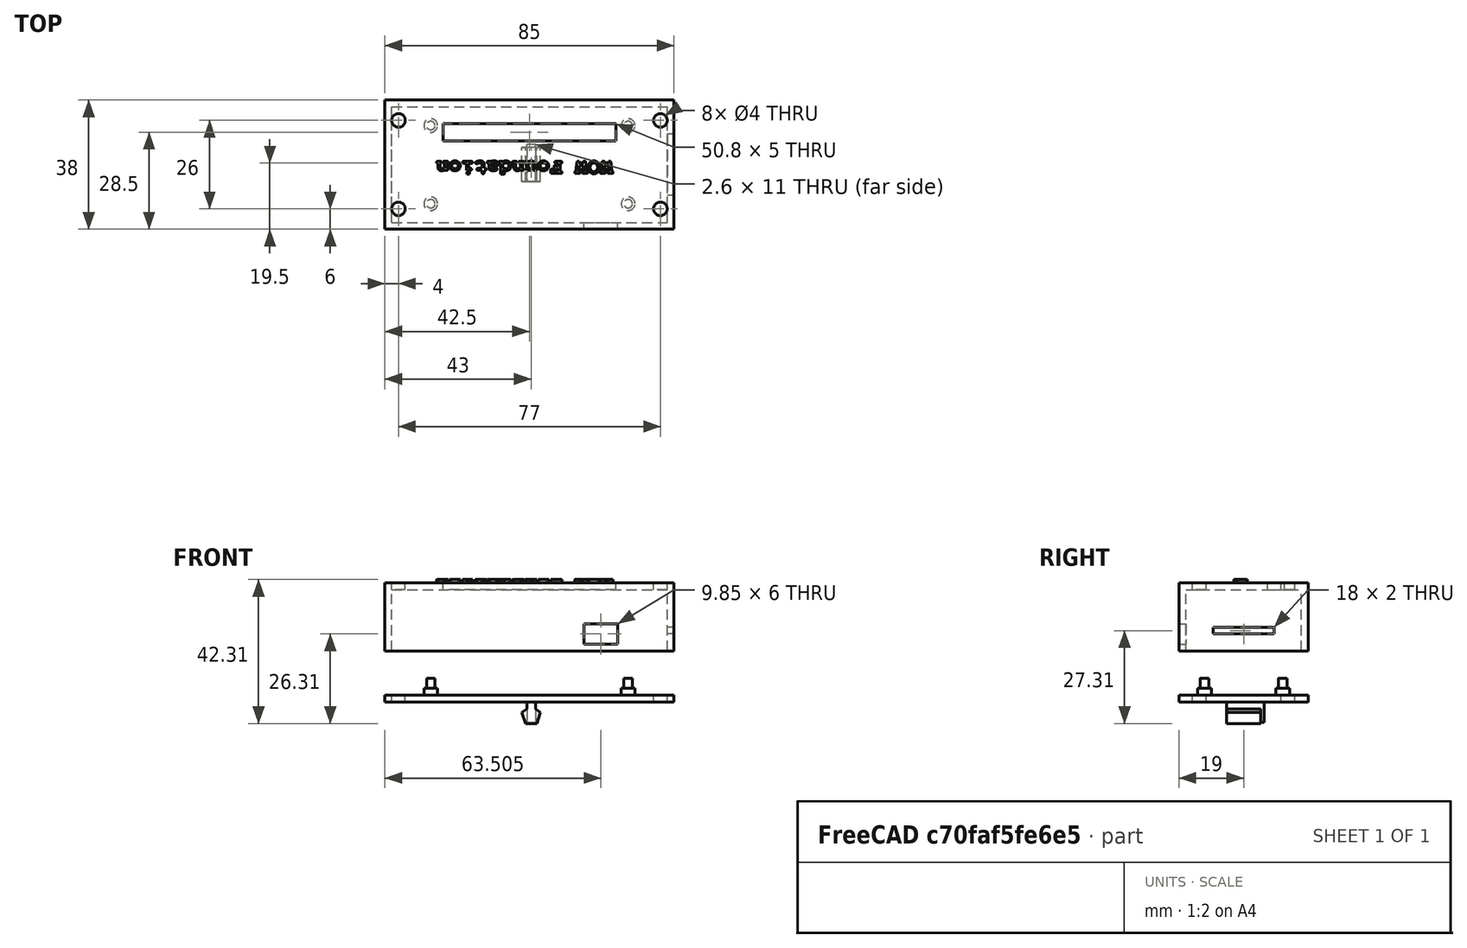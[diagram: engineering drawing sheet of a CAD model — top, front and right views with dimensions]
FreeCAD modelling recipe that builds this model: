
FCSTD DOCUMENT  (FreeCAD 0.18.1R)
Label: picase
License: All rights reserved
LicenseURL: http://en.wikipedia.org/wiki/All_rights_reserved
objects: Part::Cylinder×16, Part::Box×9, Part::MultiFuse×6, Part::Cut×6, Part::Extrusion×2, Part::Part2DObjectPython×1, Part::RegularPolygon×1
note: 41 computed .brp shape members not serialized (recipe doc carries the construction recipe); baked Part::Feature solids carry a one-line shape summary decoded from their .brp

FEATURE [Part::Box] Box  label="Cube"
  AttacherType = Attacher::AttachEngine3D
  Height = 2
  Length = 65
  Placement = pos=(0,-4,0) rot=(0,0,1;0rad)
  Width = 38
FEATURE [Part::Cylinder] Cylinder
  Angle = 360
  AttacherType = Attacher::AttachEngine3D
  Height = 5
  Placement = pos=(3.5,3.5,2) rot=(0,0,1;0rad)
  Radius = 1.25
FEATURE [Part::Cylinder] Cylinder001
  Angle = 360
  AttacherType = Attacher::AttachEngine3D
  Height = 5
  Placement = pos=(3.5,26.5,2) rot=(0,0,1;0rad)
  Radius = 1.25
FEATURE [Part::Cylinder] Cylinder002
  Angle = 360
  AttacherType = Attacher::AttachEngine3D
  Height = 5
  Placement = pos=(61.5,26.5,2) rot=(0,0,1;0rad)
  Radius = 1.25
FEATURE [Part::Cylinder] Cylinder003
  Angle = 360
  AttacherType = Attacher::AttachEngine3D
  Height = 5
  Placement = pos=(61.5,3.5,2) rot=(0,0,1;0rad)
  Radius = 1.25
FEATURE [Part::Box] Box001  label="Cube001"
  AttacherType = Attacher::AttachEngine3D
  Height = 2
  Length = 10
  Placement = pos=(-10,-4,0) rot=(0,0,1;0rad)
  Width = 38
FEATURE [Part::Box] Box002  label="Cube002"
  AttacherType = Attacher::AttachEngine3D
  Height = 2
  Length = 10
  Placement = pos=(65,-4,0) rot=(0,0,1;0rad)
  Width = 38
FEATURE [Part::Cylinder] Cylinder004
  Angle = 360
  AttacherType = Attacher::AttachEngine3D
  Height = 2
  Placement = pos=(3.5,3.5,2) rot=(0,0,1;0rad)
  Radius = 2
FEATURE [Part::Cylinder] Cylinder005
  Angle = 360
  AttacherType = Attacher::AttachEngine3D
  Height = 2
  Placement = pos=(3.5,26.5,2) rot=(0,0,1;0rad)
  Radius = 2
FEATURE [Part::Cylinder] Cylinder006
  Angle = 360
  AttacherType = Attacher::AttachEngine3D
  Height = 2
  Placement = pos=(61.5,26.5,2) rot=(0,0,1;0rad)
  Radius = 2
FEATURE [Part::Cylinder] Cylinder007
  Angle = 360
  AttacherType = Attacher::AttachEngine3D
  Height = 2
  Placement = pos=(61.5,3.5,2) rot=(0,0,1;0rad)
  Radius = 2
FEATURE [Part::MultiFuse] Fusion  label="Fusion - PI0W Base"
  Shapes = -> [Box,Cylinder003,Cylinder001,Box002,Cylinder002,Box001,Cylinder,Cylinder004,Cylinder005,Cylinder007,Cylinder006]
FEATURE [Part::Box] Box003  label="Micro-B USB"
  AttacherType = Attacher::AttachEngine3D
  Height = 6
  Length = 9.85
  Placement = pos=(48.58,-41,2) rot=(0,0,1;0rad)
  Width = 7
FEATURE [Part::Box] Box004  label="GPIOHeader"
  AttacherType = Attacher::AttachEngine3D
  Height = 10
  Length = 50.8
  Placement = pos=(7.1,-15,16) rot=(0,0,1;0rad)
  Width = 5
FEATURE [Part::Box] Box005  label="camera-cable-slot"
  AttacherType = Attacher::AttachEngine3D
  Height = 2
  Length = 18
  Placement = pos=(76,-31,5) rot=(0,0,1;1.5708rad)
  Width = 4
FEATURE [Part::Box] Box006  label="Pitop"
  AttacherType = Attacher::AttachEngine3D
  Height = 20
  Length = 85
  Placement = pos=(-10,-41,0) rot=(0,0,1;0rad)
  Width = 38
FEATURE [Part::Box] Box007  label="pihollow"
  AttacherType = Attacher::AttachEngine3D
  Height = 18
  Length = 81
  Placement = pos=(-8,-39,0) rot=(0,0,1;0rad)
  Width = 34
FEATURE [Part::Part2DObjectPython] ShapeString002  # Draft 2D object (typed FeaturePython)
  FontFile = <path>
  Placement = pos=(5,-40,11) rot=(0,0,1;0rad)
  Size = 2
  String = WOW Foundation
  Tracking = 0
FEATURE [Part::Extrusion] Extrude
  Base = -> ShapeString002
  Dir = (0,0,1)
  DirMode = 2
  FaceMakerClass = Part::FaceMakerBullseye
  LengthFwd = 2
  LengthRev = 0
  Placement = pos=(62,-61,8) rot=(0,0,1;3.14159rad)
  Solid = false
  Symmetric = false
FEATURE [Part::Box] Box008  label="Cube003"
  AttacherType = Attacher::AttachEngine3D
  Height = 8
  Length = 11
  Placement = pos=(0,5.7,-3) rot=(0,0,1;0rad)
  Width = 2.6
FEATURE [Part::RegularPolygon] RegularPolygon001  label="Regular polygon001"
  AttacherType = Attacher::AttachEngine3D
  Circumradius = 2.85
  Placement = pos=(-3,7,0) rot=(0,0,1;0rad)
  Polygon = 5
FEATURE [Part::Extrusion] Extrude001
  Base = -> RegularPolygon001
  Dir = (0,0,1)
  DirMode = 2
  FaceMakerClass = Part::FaceMakerBullseye
  LengthFwd = 10
  LengthRev = 0
  Placement = pos=(0,0,0) rot=(0,1,0;1.5708rad)
  Solid = true
  Symmetric = false
FEATURE [Part::MultiFuse] Fusion001
  Placement = pos=(26,10,-1) rot=(0.707107,0.707107,0;-3.14159rad)
  Shapes = -> [Extrude001,Box008]
FEATURE [Part::Cylinder] Cylinder008
  Angle = 360
  AttacherType = Attacher::AttachEngine3D
  Height = 5
  Placement = pos=(-6,2,-1) rot=(0,0,1;0rad)
  Radius = 2
FEATURE [Part::Cylinder] Cylinder009
  Angle = 360
  AttacherType = Attacher::AttachEngine3D
  Height = 5
  Placement = pos=(-6,28,-1) rot=(0,0,1;0rad)
  Radius = 2
FEATURE [Part::Cylinder] Cylinder010
  Angle = 360
  AttacherType = Attacher::AttachEngine3D
  Height = 5
  Placement = pos=(71,28,-1) rot=(0,0,1;0rad)
  Radius = 2
FEATURE [Part::Cylinder] Cylinder011
  Angle = 360
  AttacherType = Attacher::AttachEngine3D
  Height = 5
  Placement = pos=(71,2,-1) rot=(0,0,1;0rad)
  Radius = 2
FEATURE [Part::MultiFuse] Fusion002
  Shapes = -> [Cylinder008,Cylinder009,Cylinder010,Cylinder011]
FEATURE [Part::Cut] Cut004
  Base = -> Fusion
  Tool = -> Fusion002
FEATURE [Part::MultiFuse] Fusion003  label="PiBase"
  Shapes = -> [Cut004,Fusion001]
FEATURE [Part::Cylinder] Cylinder012
  Angle = 360
  AttacherType = Attacher::AttachEngine3D
  Height = 5
  Placement = pos=(-6,2,-1) rot=(0,0,1;0rad)
  Radius = 2
FEATURE [Part::Cylinder] Cylinder013
  Angle = 360
  AttacherType = Attacher::AttachEngine3D
  Height = 5
  Placement = pos=(-6,28,-1) rot=(0,0,1;0rad)
  Radius = 2
FEATURE [Part::Cylinder] Cylinder014
  Angle = 360
  AttacherType = Attacher::AttachEngine3D
  Height = 5
  Placement = pos=(71,28,-1) rot=(0,0,1;0rad)
  Radius = 2
FEATURE [Part::Cylinder] Cylinder015
  Angle = 360
  AttacherType = Attacher::AttachEngine3D
  Height = 5
  Placement = pos=(71,2,-1) rot=(0,0,1;0rad)
  Radius = 2
FEATURE [Part::MultiFuse] Fusion005
  Placement = pos=(0,-37,17) rot=(0,0,1;0rad)
  Shapes = -> [Cylinder012,Cylinder013,Cylinder014,Cylinder015]
FEATURE [Part::Cut] Cut
  Base = -> Box006
  Tool = -> Box007
FEATURE [Part::Cut] Cut005
  Base = -> Cut
  Tool = -> Box003
FEATURE [Part::Cut] Cut006
  Base = -> Cut005
  Tool = -> Box005
FEATURE [Part::Cut] Cut007
  Base = -> Cut006
  Tool = -> Box004
FEATURE [Part::Cut] Cut008
  Base = -> Cut007
  Tool = -> Fusion005
FEATURE [Part::MultiFuse] Fusion006  label="PiTop"
  Placement = pos=(0,37,15) rot=(0,0,1;0rad)
  Shapes = -> [Cut008,Extrude]
note: 1 file-system path scrubbed to <path> (originals preserved in the JSON sidecar)
